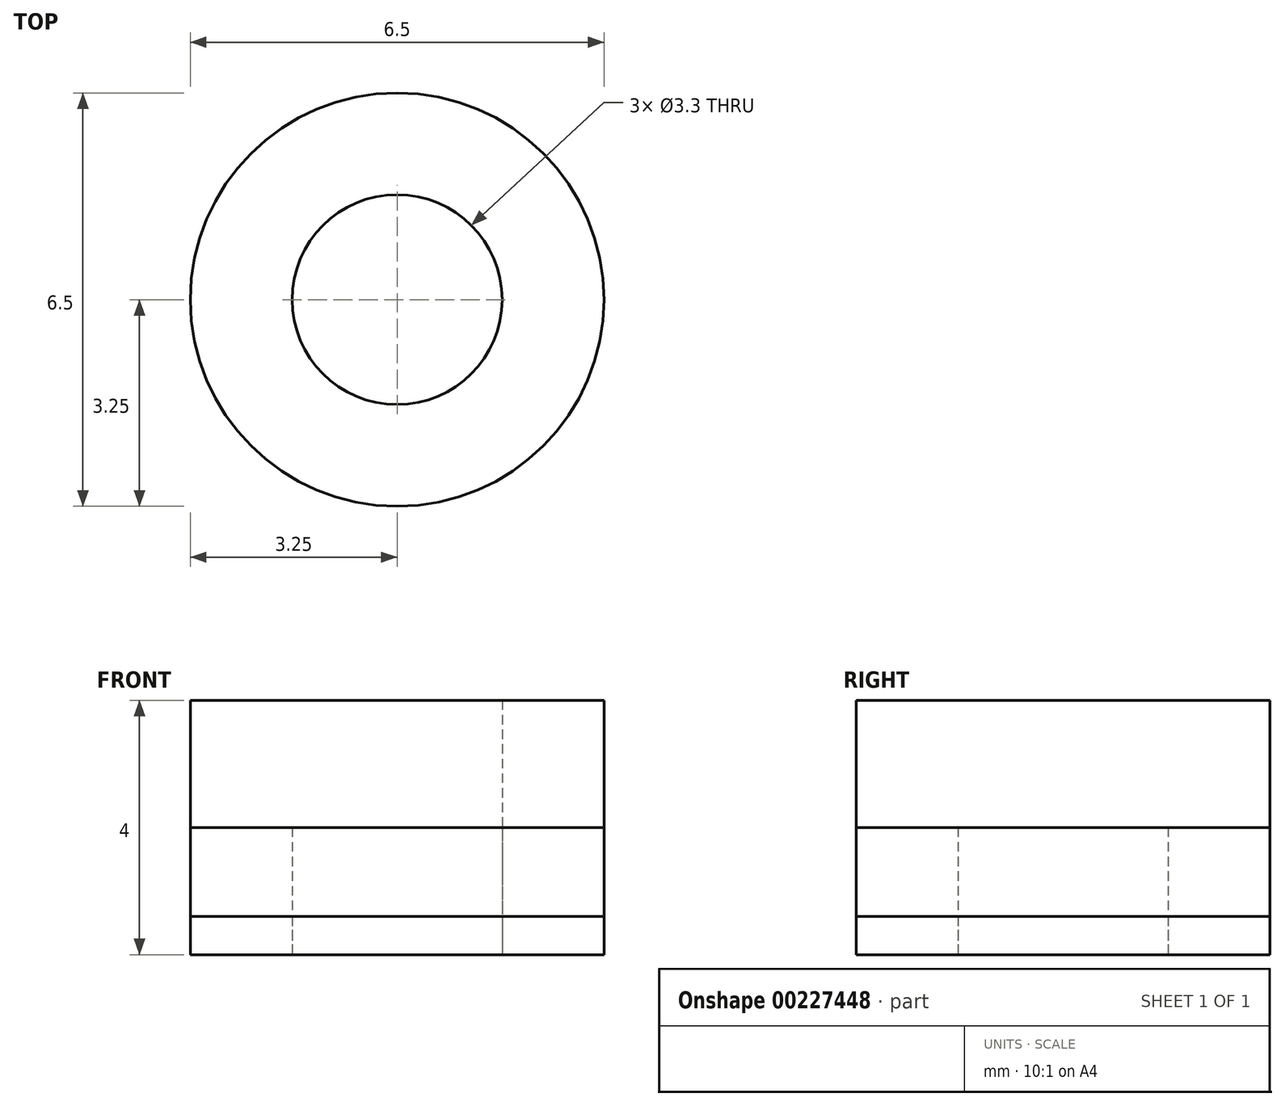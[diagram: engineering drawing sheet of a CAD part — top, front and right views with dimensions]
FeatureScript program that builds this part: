
annotation { "Feature Type Name" : "Feature", "Feature Type Description" : "" }
export const myFeature = defineFeature(function(context is Context, id is Id, definition is map)
    precondition{}
    {
        {
            var Q0;
            Q0=qCreatedBy(makeId("Top.planeOp"),FACE);
            var sketch = newSketch(context, id + "F0", { "sketchPlane" : qUnion([Q0])});
            skCircle(sketch, "E0", {"center": v(0, 0) * mm, "radius": 1.65 * mm});
            skCircle(sketch, "E1", {"center": v(0, 0) * mm, "radius": 3.25 * mm});
            skSolve(sketch);
        }
        {
            var Q0;
            Q0=makeQuery(id+"F0.imprint","IMPRINT",FACE,{"disambiguationData":[TD([[makeQuery(id+"F0.imprint","IMPRINT",EDGE,{"derivedFrom":sQuery(id+"F0.wireOp",EDGE,"E0")}),-1.0]])]});
            extrude(context, id + "F1", {"entities" : qUnion([Q0]), "depth" : 0.6 * mm, "offsetDistance" : 25 * mm});
        }
        {
            var Q0;
            Q0 = qSketchRegion(id + "F0", true);
            extrude(context, id + "F2", {"entities" : qUnion([Q0]), "depth" : 2 * mm, "offsetDistance" : 25 * mm});
        }
        {
            var Q0;
            Q0=makeQuery(id+"F2.opExtrude","CAP_FACE",FACE,{"disambiguationData":[OSD([sQuery(id+"F0.wireOp",EDGE,"E0"),sQuery(id+"F0.wireOp",EDGE,"E1")])],"isStart":true});
            extrude(context, id + "F3", {"entities" : qUnion([Q0]), "oppositeDirection" : true, "depth" : 4 * mm, "offsetDistance" : 25 * mm});
        }
    });
